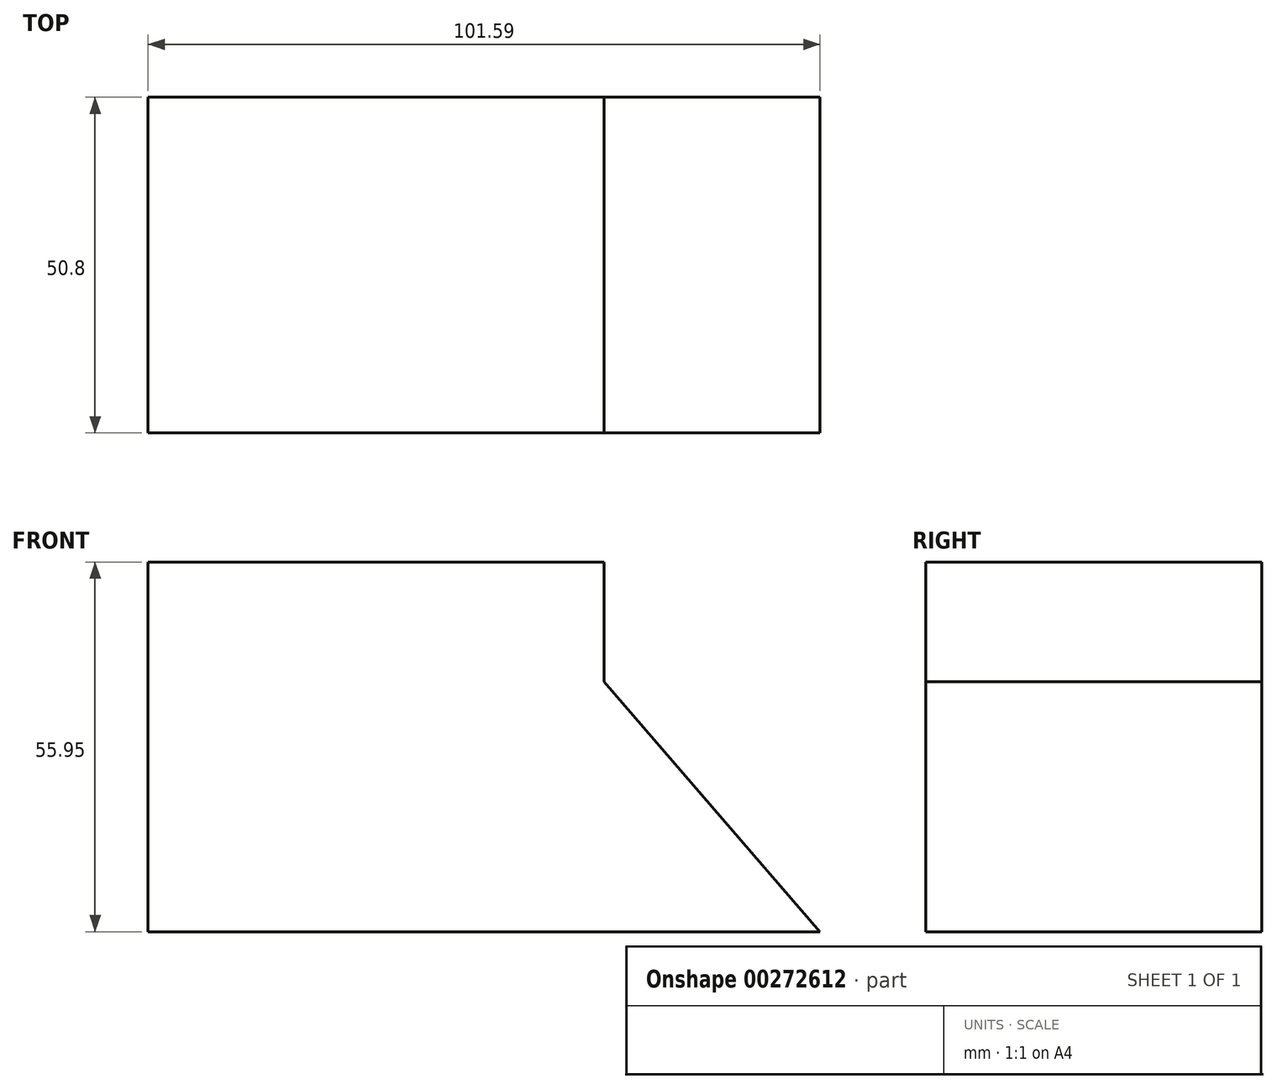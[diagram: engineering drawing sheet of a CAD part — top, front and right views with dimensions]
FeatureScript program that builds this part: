
annotation { "Feature Type Name" : "Feature", "Feature Type Description" : "" }
export const myFeature = defineFeature(function(context is Context, id is Id, definition is map)
    precondition{}
    {
        {
            var Q0;
            Q0=qCreatedBy(makeId("Front.planeOp"),FACE);
            var sketch = newSketch(context, id + "F0", { "sketchPlane" : qUnion([Q0])});
            skLineSegment(sketch, "E0.bottom", {"start": v(-36.28, 55.95) * mm, "end": v(32.65, 55.95) * mm});
            skLineSegment(sketch, "E0.top", {"start": v(-36.28, 0) * mm, "end": v(32.65, 0) * mm});
            skLineSegment(sketch, "E0.left", {"start": v(-36.28, 55.95) * mm, "end": v(-36.28, 0) * mm});
            skLineSegment(sketch, "E0.right", {"start": v(32.65, 55.95) * mm, "end": v(32.65, 0) * mm});
            skSolve(sketch);
        }
        {
            var Q0;
            Q0 = qSketchRegion(id + "F0", true);
            extrude(context, id + "F1", {"entities" : qUnion([Q0]), "depth" : 50.8 * mm});
        }
        {
            var Q0;
            Q0=makeQuery(id+"F1.opExtrude","CAP_FACE",FACE,{"disambiguationData":[OSD([sQuery(id+"F0.wireOp",EDGE,"E0.bottom"),sQuery(id+"F0.wireOp",EDGE,"E0.top"),sQuery(id+"F0.wireOp",EDGE,"E0.left"),sQuery(id+"F0.wireOp",EDGE,"E0.right")])],"isStart":false});
            var sketch = newSketch(context, id + "F2", { "sketchPlane" : qUnion([Q0])});
            skLineSegment(sketch, "E1", {"start": v(32.65, 37.8) * mm, "end": v(65.3, 0) * mm});
            skLineSegment(sketch, "E2", {"start": v(65.3, 0) * mm, "end": v(32.65, 0) * mm});
            skLineSegment(sketch, "E3", {"start": v(32.65, 0) * mm, "end": v(32.65, 37.8) * mm});
            skSolve(sketch);
        }
        {
            var Q0;
            Q0 = qSketchRegion(id + "F2", true);
            extrude(context, id + "F3", {"entities" : qUnion([Q0]), "operationType" : NewBodyOperationType.ADD, "oppositeDirection" : true, "depth" : 50.8 * mm});
        }
    });
